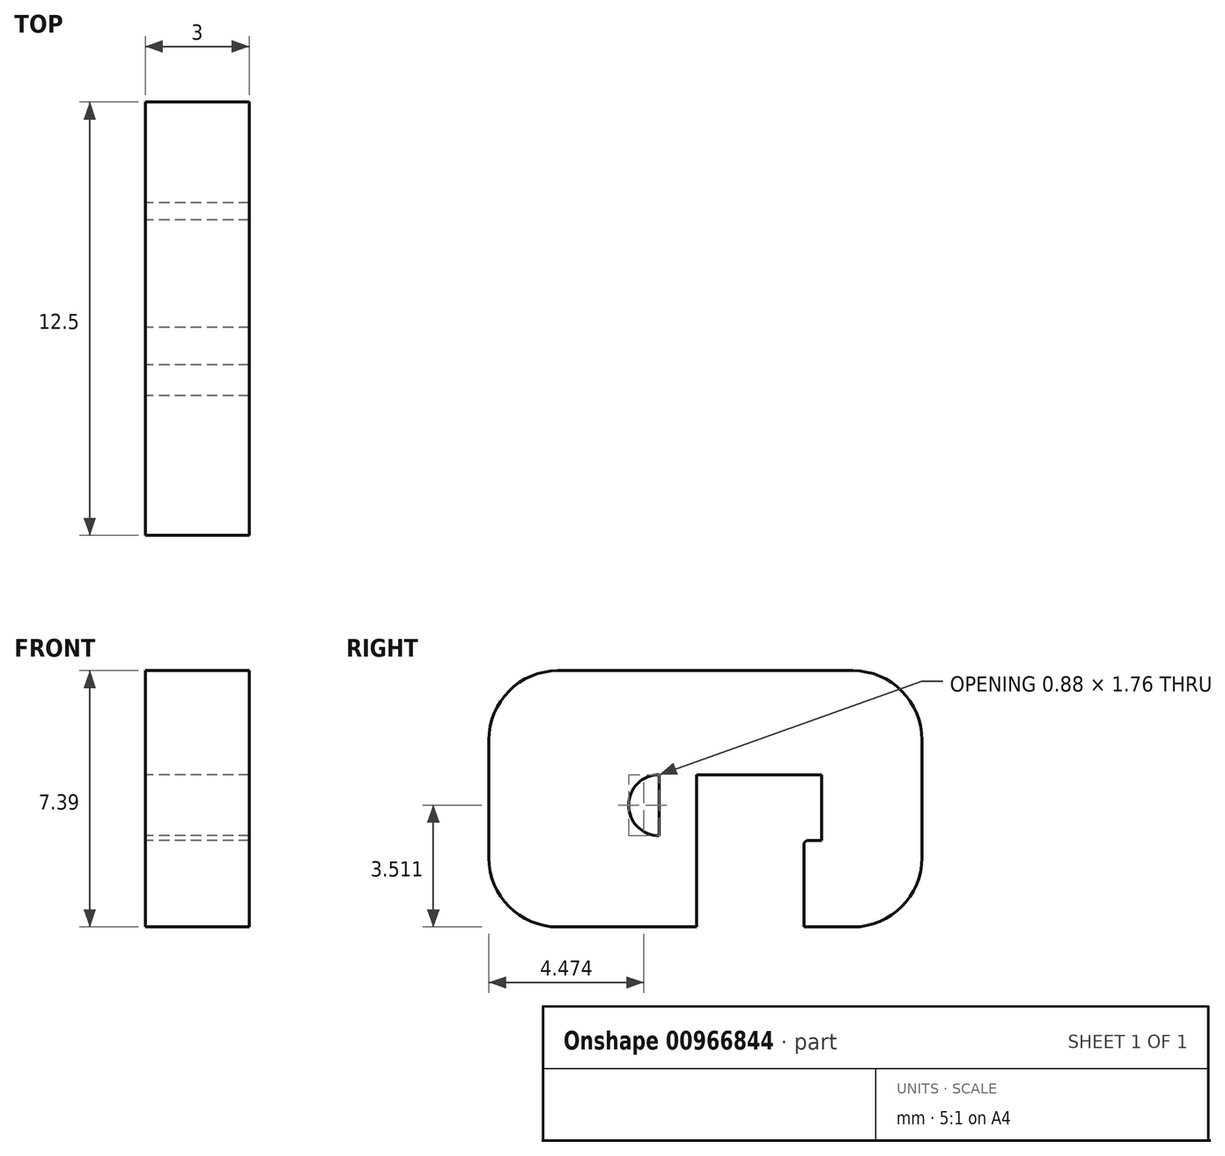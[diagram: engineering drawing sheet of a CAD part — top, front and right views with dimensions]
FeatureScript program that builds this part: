
annotation { "Feature Type Name" : "Feature", "Feature Type Description" : "" }
export const myFeature = defineFeature(function(context is Context, id is Id, definition is map)
    precondition{}
    {
        {
            var Q0;
            Q0=qCreatedBy(makeId("Right.planeOp"),FACE);
            var sketch = newSketch(context, id + "F0", { "sketchPlane" : qUnion([Q0])});
            skLineSegment(sketch, "E0", {"start": v(0, 2) * mm, "end": v(0, 5.4) * mm});
            skLineSegment(sketch, "E1", {"start": v(-2, 7.4) * mm, "end": v(-10.5, 7.4) * mm});
            skLineSegment(sketch, "E2", {"start": v(-12.5, 5.4) * mm, "end": v(-12.5, 2) * mm});
            skLineSegment(sketch, "E3", {"start": v(-6.5, 0) * mm, "end": v(-6.5, 4.4) * mm});
            skLineSegment(sketch, "E4", {"start": v(-6.5, 4.4) * mm, "end": v(-2.9, 4.4) * mm});
            skLineSegment(sketch, "E5", {"start": v(-2.9, 4.4) * mm, "end": v(-2.9, 2.5) * mm});
            skLineSegment(sketch, "E6", {"start": v(-2.9, 0) * mm, "end": v(-2, 0) * mm});
            skPoint(sketch, "E7", {"position": v(-2.9, 2.5) * mm});
            skLineSegment(sketch, "E8", {"start": v(-2.9, 2.5) * mm, "end": v(-3.3, 2.5) * mm});
            skLineSegment(sketch, "E9", {"start": v(-3.4, 2.4) * mm, "end": v(-3.4, 0) * mm});
            skLineSegment(sketch, "E10", {"start": v(-3.4, 0) * mm, "end": v(-2.9, 0) * mm});
            skLineSegment(sketch, "E11", {"start": v(-10.5, 0) * mm, "end": v(-6.5, 0) * mm});
            skPoint(sketch, "E12.centerSnap0", {"position": v(-9.5, 0) * mm});
            skPoint(sketch, "E12.centerSnap1", {"position": v(-12.5, 3.7) * mm});
            skPoint(sketch, "E13.visualSharp", {"position": v(-3.4, 2.5) * mm});
            skArc(sketch, "E13.filletArc", {"start": v(-3.3, 2.5) * mm, "mid": v(-3.37, 2.46) * mm, "end": v(-3.4, 2.4) * mm});
            skPoint(sketch, "E14.visualSharp", {"position": v(-12.5, 7.4) * mm});
            skArc(sketch, "E14.filletArc", {"start": v(-10.5, 7.4) * mm, "mid": v(-11.91, 6.8) * mm, "end": v(-12.5, 5.4) * mm});
            skPoint(sketch, "E15.visualSharp", {"position": v(-12.5, 0) * mm});
            skArc(sketch, "E15.filletArc", {"start": v(-12.5, 2) * mm, "mid": v(-11.91, 0.59) * mm, "end": v(-10.5, 0) * mm});
            skPoint(sketch, "E16.visualSharp", {"position": v(0, 7.4) * mm});
            skArc(sketch, "E16.filletArc", {"start": v(0, 5.4) * mm, "mid": v(-0.59, 6.8) * mm, "end": v(-2, 7.4) * mm});
            skPoint(sketch, "E17.visualSharp", {"position": v(0, 0) * mm});
            skArc(sketch, "E17.filletArc", {"start": v(-2, 0) * mm, "mid": v(-0.59, 0.59) * mm, "end": v(0, 2) * mm});
            skLineSegment(sketch, "E18", {"start": v(-6.5, 4.4) * mm, "end": v(-7.59, 4.4) * mm});
            skLineSegment(sketch, "E19", {"start": v(-7.59, 4.4) * mm, "end": v(-7.59, 2.63) * mm});
            skLineSegment(sketch, "E20", {"start": v(-7.59, 2.63) * mm, "end": v(-6.5, 2.63) * mm});
            skArc(sketch, "E21", {"start": v(-7.59, 4.4) * mm, "mid": v(-8.47, 3.51) * mm, "end": v(-7.59, 2.63) * mm});
            skSolve(sketch);
        }
        {
            var Q0;
            Q0 = qSketchRegion(id + "F0", true);
            extrude(context, id + "F1", {"entities" : qUnion([Q0]), "depth" : 3 * mm, "offsetDistance" : 25 * mm});
        }
    });
